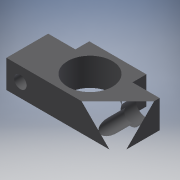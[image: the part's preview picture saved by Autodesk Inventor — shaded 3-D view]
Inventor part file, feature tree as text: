
AUTODESK INVENTOR PART (.ipt)
format: ipt  version: 2016 (Build 200138000, 138)  size: 143,360 bytes
history: native  units: mm
features: other x14, sketch x4, hole x3, extrude x1
ambient origin geometry x8: Origin, YZ Plane, XZ Plane, XY Plane, X Axis, Y Axis, Z Axis, Center Point
bodies: Solid1 (feature_tree)
feature tree (22):
  extrude  "Extrusion1"  TaperAngle=0.0deg  [1 undecoded]
  hole  "Hole1"  [1 undecoded]
  hole  "Hole2"  [1 undecoded]
  hole  "Hole3"  [1 undecoded]
  other  "bf_1_XY"
  other  "bf_1_YZ"
  other  "bf_1_ZX"
  other  "bf_1_X"
  other  "bf_1_Y"
  other  "bf_1_Z"
  other  "bf_1_Center"
  other  "bf_2x_XY"
  other  "bf_2x_YZ"
  other  "bf_2x_ZX"
  other  "bf_2x_Y"
  other  "bf_2x_Z"
  other  "bf_2x_X"
  other  "bf_2x_Center"
  sketch  "Sketch_1"  dims[d0=20.0mm d1=0.0mm]
  sketch  "Sketch2"  dims[d2=9.0mm d3=6.0mm d4=14.0mm d5=11.0mm d6=90.0deg d7=38.0mm d8=0.0mm]
  sketch  "Sketch3"  dims[d9=9.0mm d10=6.0mm d11=14.0mm d12=11.0mm d13=90.0deg d14=38.0mm d15=0.0mm]
  sketch  "Sketch4"  dims[d16=32.0mm d17=6.0mm d18=4.0mm d19=2.0mm d20=90.0deg d21=20.0mm d22=0.0mm d23=0.0mm d24=80.0mm d25=40.0mm d26=10.0mm d27=10.0mm d28=41.0mm d29=20.0mm d30=10.0mm d31=10.0mm]
note: 4 required parameter values undecoded (feature->parameter linkage not recoverable at this tier; creation-order binding heuristic only, values carry confidence <= 0.55)
